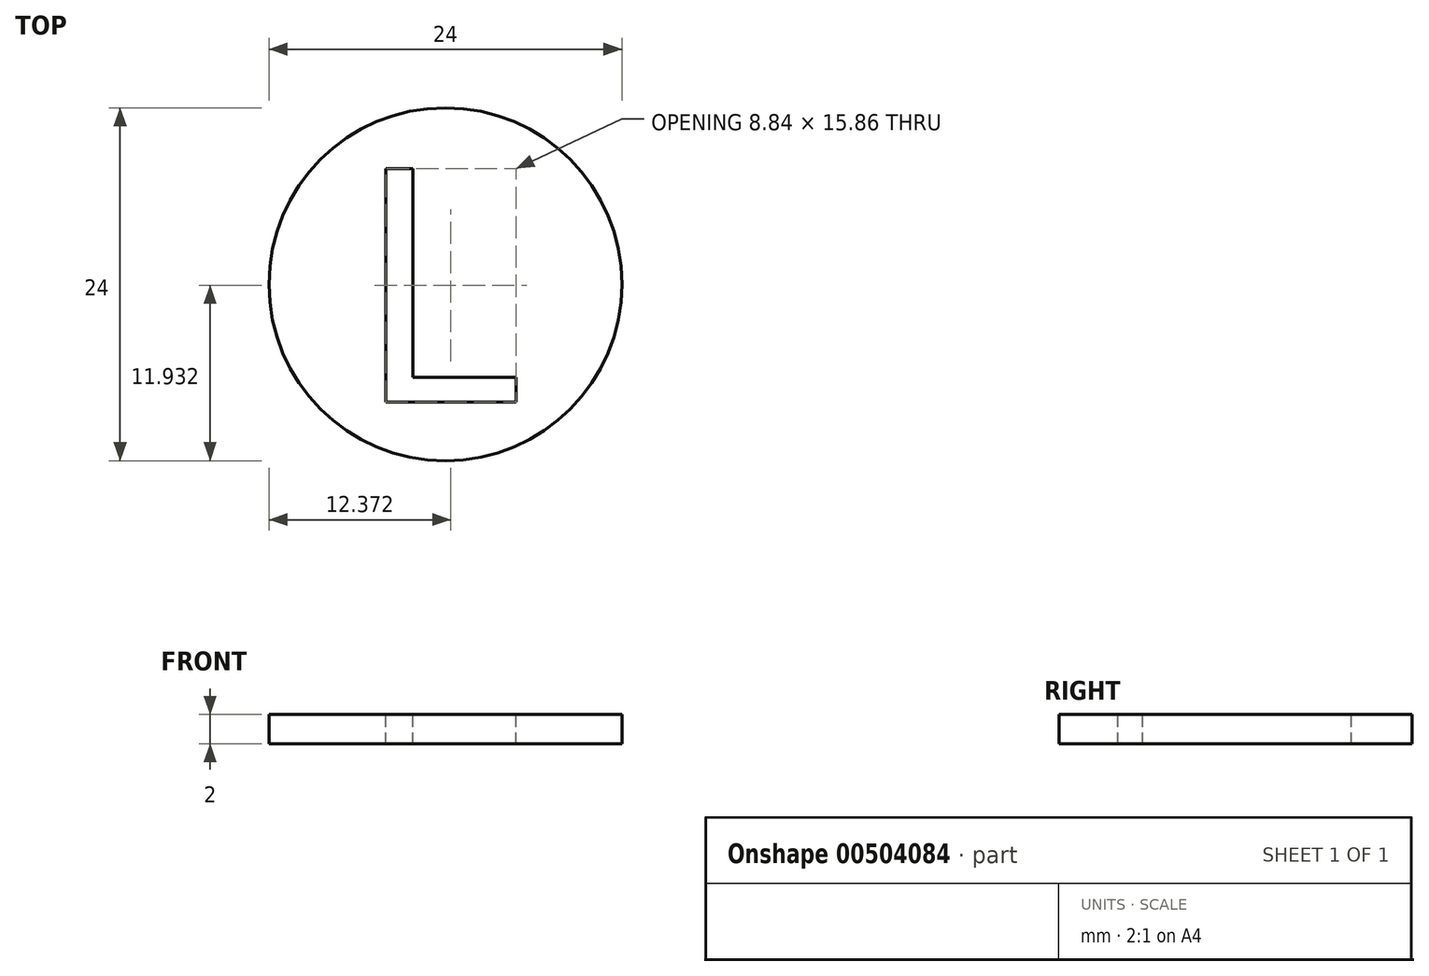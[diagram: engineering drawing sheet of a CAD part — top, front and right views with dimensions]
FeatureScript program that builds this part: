
annotation { "Feature Type Name" : "Feature", "Feature Type Description" : "" }
export const myFeature = defineFeature(function(context is Context, id is Id, definition is map)
    precondition{}
    {
        {
            var Q0;
            Q0=qCreatedBy(makeId("Top.planeOp"),FACE);
            var sketch = newSketch(context, id + "F0", { "sketchPlane" : qUnion([Q0])});
            skCircle(sketch, "E0", {"center": v(0, 0) * mm, "radius": 12 * mm});
            skSolve(sketch);
        }
        {
            var Q0;
            Q0=qSketchRegion(id+"F0",true);
            extrude(context, id + "F1", {"entities" : qUnion([Q0]), "depth" : 2 * mm});
        }
        {
            var Q0;
            Q0=makeQuery(id+"F1.opExtrude","CAP_FACE",FACE,{"disambiguationData":[OSD([sQuery(id+"F0.wireOp",EDGE,"E0")])],"isStart":false});
            var sketch = newSketch(context, id + "F2", { "sketchPlane" : qUnion([Q0])});
            skText(sketch, "E1", { "text": "L", "fontName": "OpenSans-Regular.ttf"});
            skPoint(sketch, "E2", {"position": v(6.23, 0) * mm});
            const initialGuessF2  = {"E1": [-0.00623, -0.008, 1, 0, 0.016]};
            skSetInitialGuess(sketch, initialGuessF2);
            skSolve(sketch);
        }
        {
            var Q0;
            Q0 = qSketchRegion(id + "F2", true);
            extrude(context, id + "F3", {"entities" : qUnion([Q0]), "operationType" : NewBodyOperationType.REMOVE, "oppositeDirection" : true, "depth" : 25 * mm, "offsetDistance" : 25 * mm});
        }
    });
